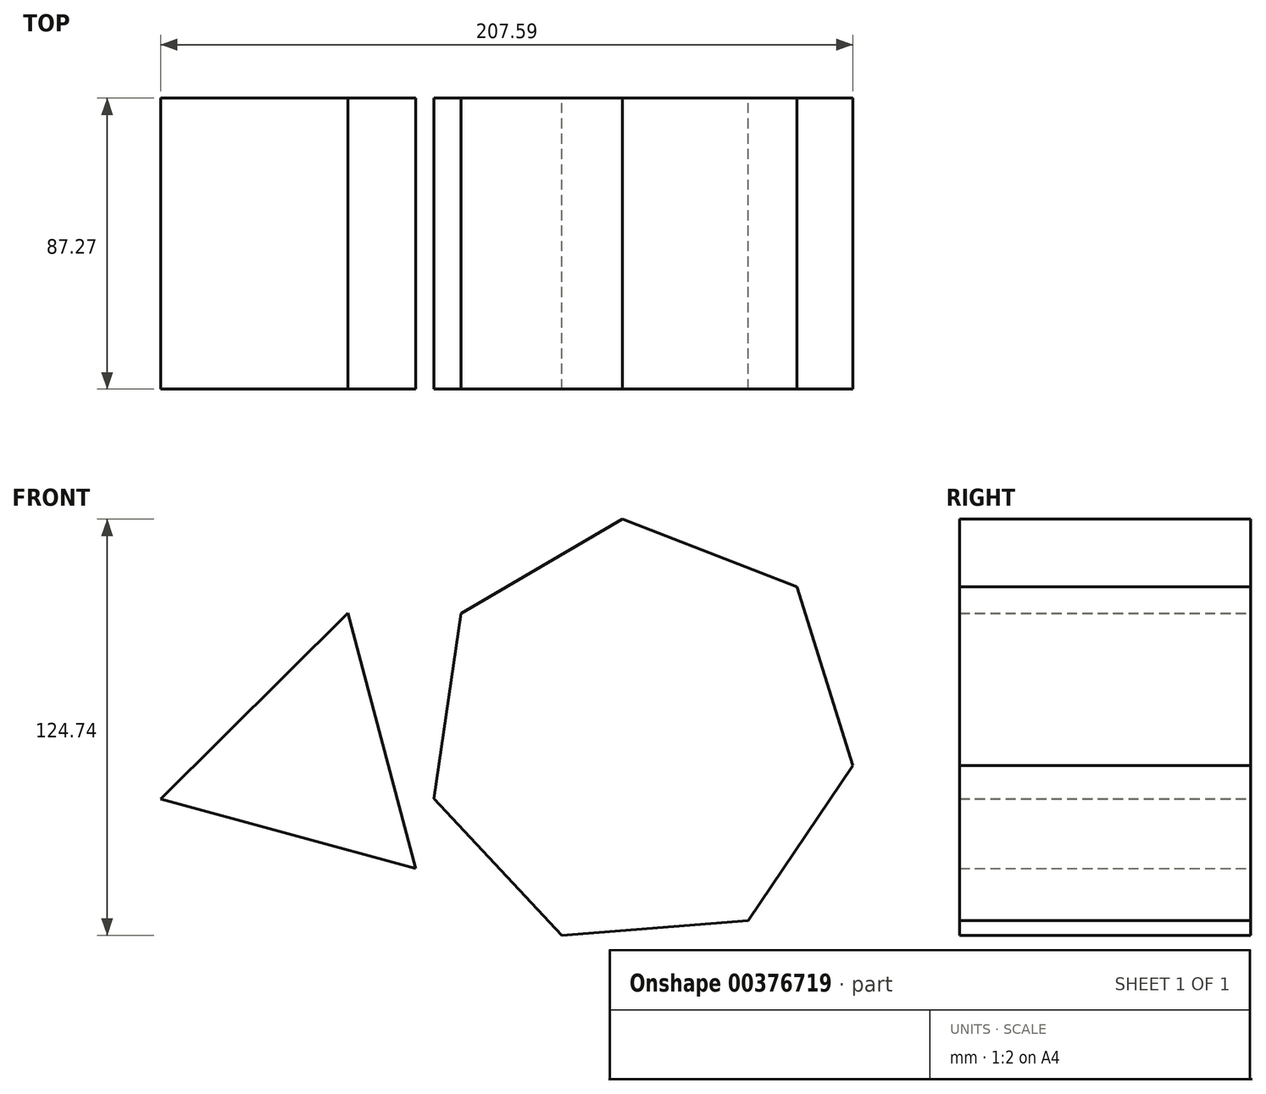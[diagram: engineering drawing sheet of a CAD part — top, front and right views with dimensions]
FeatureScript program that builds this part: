
annotation { "Feature Type Name" : "Feature", "Feature Type Description" : "" }
export const myFeature = defineFeature(function(context is Context, id is Id, definition is map)
    precondition{}
    {
        {
            var Q0;
            Q0=qCreatedBy(makeId("Front.planeOp"),FACE);
            var sketch = newSketch(context, id + "F0", { "sketchPlane" : qUnion([Q0])});
            skCircle(sketch, "E0.cCircle", {"center": v(57.64, -8.43) * mm, "radius": 58.25 * mm, "construction": true});
            skLineSegment(sketch, "E0.0", {"start": v(-4.06, -27.76) * mm, "end": v(4.06, 27.76) * mm});
            skLineSegment(sketch, "E0.1", {"start": v(4.06, 27.76) * mm, "end": v(52.52, 56.02) * mm});
            skLineSegment(sketch, "E0.2", {"start": v(52.52, 56.02) * mm, "end": v(104.84, 35.75) * mm});
            skLineSegment(sketch, "E0.3", {"start": v(104.84, 35.75) * mm, "end": v(121.6, -17.79) * mm});
            skLineSegment(sketch, "E0.4", {"start": v(121.6, -17.79) * mm, "end": v(90.2, -64.28) * mm});
            skLineSegment(sketch, "E0.5", {"start": v(90.2, -64.28) * mm, "end": v(34.28, -68.72) * mm});
            skLineSegment(sketch, "E0.6", {"start": v(34.28, -68.72) * mm, "end": v(-4.06, -27.76) * mm});
            skPoint(sketch, "E0.0.midPoint", {"position": v(0, 0) * mm});
            skCircle(sketch, "E1.cCircle", {"center": v(-41.77, -16.21) * mm, "radius": 22.87 * mm, "construction": true});
            skLineSegment(sketch, "E1.0", {"start": v(-85.98, -27.93) * mm, "end": v(-29.82, 27.93) * mm});
            skLineSegment(sketch, "E1.1", {"start": v(-29.82, 27.93) * mm, "end": v(-9.52, -48.64) * mm});
            skLineSegment(sketch, "E1.2", {"start": v(-9.52, -48.64) * mm, "end": v(-85.98, -27.93) * mm});
            skPoint(sketch, "E1.0.midPoint", {"position": v(-57.9, 0) * mm});
            skSolve(sketch);
        }
        {
            var Q0;
            Q0 = qSketchRegion(id + "F0", true);
            extrude(context, id + "F1", {"entities" : qUnion([Q0]), "depth" : 87.27 * mm});
        }
    });
